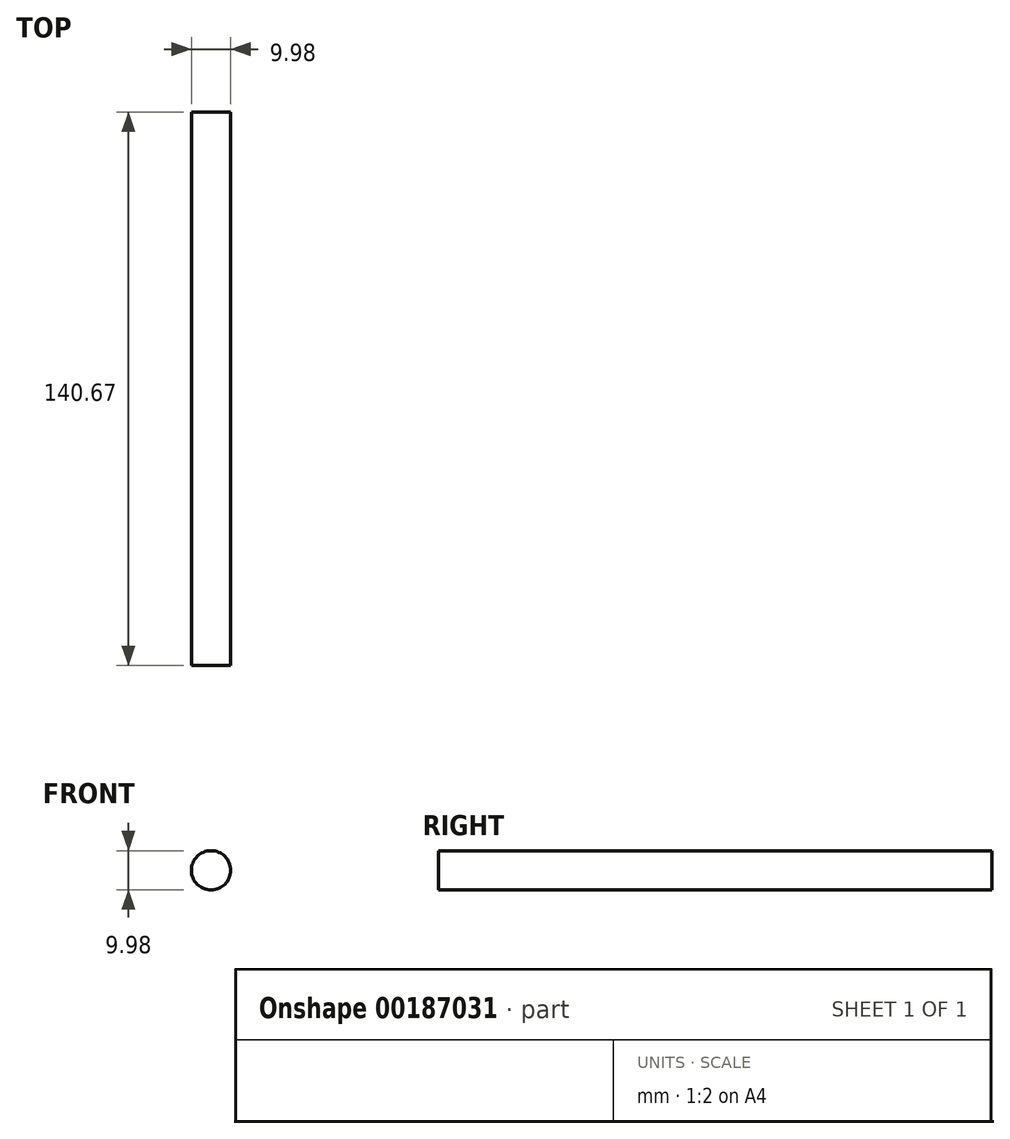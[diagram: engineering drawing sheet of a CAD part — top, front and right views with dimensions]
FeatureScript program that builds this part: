
annotation { "Feature Type Name" : "Feature", "Feature Type Description" : "" }
export const myFeature = defineFeature(function(context is Context, id is Id, definition is map)
    precondition{}
    {
        {
            var Q0;
            Q0=qCreatedBy(makeId("Front.planeOp"),FACE);
            var sketch = newSketch(context, id + "F0", { "sketchPlane" : qUnion([Q0])});
            skCircle(sketch, "E0", {"center": v(0, 0) * mm, "radius": 5 * mm});
            skSolve(sketch);
        }
        {
            var Q0;
            Q0 = qSketchRegion(id + "F0", true);
            extrude(context, id + "F1", {"entities" : qUnion([Q0]), "depth" : 140.67 * mm});
        }
    });
